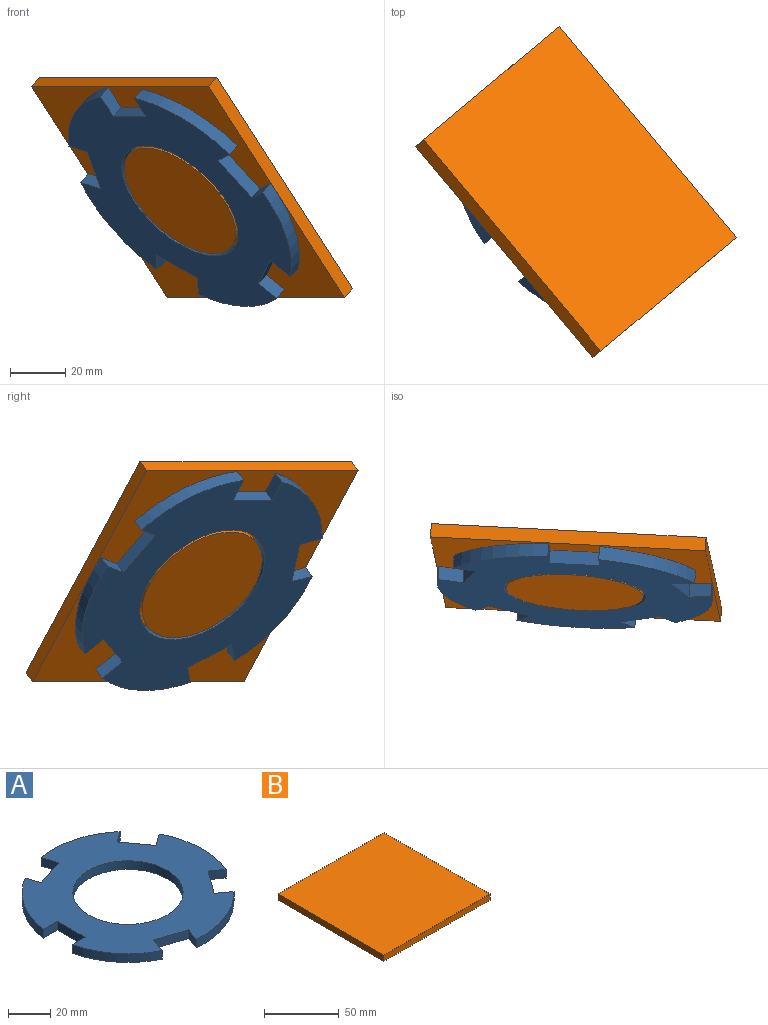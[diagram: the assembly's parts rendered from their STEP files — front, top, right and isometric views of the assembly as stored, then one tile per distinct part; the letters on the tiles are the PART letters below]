
ASSEMBLY  parts=2 mates=1
PART A: 23 faces, bbox 99.5x100x5 mm
  f0: cylinder r=50mm len=41.28mm, axis (0,0,1), area 221.2mm2, adj f2,f5,f16,f18
  f1: plane 8.16x5mm, normal (0.95,0.31,0), area 42.9mm2, adj f3,f16,f17,f18
  f2: plane 8.97x5mm, normal (-0.95,-0.31,0), area 47.1mm2, adj f0,f3,f16,f18
  f3: plane 17.56x5.71mm, normal (-0.31,0.95,0), area 92.3mm2, adj f1,f2,f16,f18
  f4: cylinder r=50mm len=42.77mm, axis (0,0,1), area 221.2mm2, adj f6,f9,f16,f18
  f5: plane 6.94x5.04mm, normal (0.59,-0.81,0), area 42.9mm2, adj f0,f7,f16,f18
  f6: plane 7.63x5.54mm, normal (-0.59,0.81,0), area 47.1mm2, adj f4,f7,f16,f18
  f7: plane 14.94x10.85mm, normal (0.81,0.59,0), area 92.3mm2, adj f5,f6,f16,f18
  f8: cylinder r=50mm len=40.07mm, axis (0,0,1), area 221.2mm2, adj f10,f13,f16,f18
  f9: plane 6.94x5.04mm, normal (-0.59,-0.81,0), area 42.9mm2, adj f4,f11,f16,f18
  f10: plane 7.63x5.54mm, normal (0.59,0.81,0), area 47.1mm2, adj f8,f11,f16,f18
  f11: plane 14.94x10.85mm, normal (0.81,-0.59,0), area 92.3mm2, adj f9,f10,f16,f18
  f12: cylinder r=50mm len=33.44mm, axis (0,0,1), area 221.2mm2, adj f14,f16,f18,f22
  f13: plane 8.16x5mm, normal (-0.95,0.31,0), area 42.9mm2, adj f8,f15,f16,f18
  f14: plane 8.97x5mm, normal (0.95,-0.31,0), area 47.1mm2, adj f12,f15,f16,f18
  f15: plane 17.56x5.71mm, normal (-0.31,-0.95,0), area 92.3mm2, adj f13,f14,f16,f18
  f16: plane 100x99.51mm, normal (0,0,1), area 4846mm2, adj f0,f1,f2,f3,f4,f5,f6,f7
  f17: cylinder r=50mm len=35.76mm, axis (0,0,1), area 221.2mm2, adj f1,f16,f18,f20
  f18: plane 100x99.51mm, normal (0,0,-1), area 4846mm2, adj f0,f1,f2,f3,f4,f5,f6,f7
  f19: cylinder r=26mm len=52mm, axis (0,0,1), area 816.8mm2, adj f16,f18
  f20: plane 9.43x5mm, normal (0,-1,0), area 47.1mm2, adj f16,f17,f18,f21
  f21: plane 18.46x5mm, normal (-1,0,0), area 92.3mm2, adj f16,f18,f20,f22
  f22: plane 8.58x5mm, normal (0,1,0), area 42.9mm2, adj f12,f16,f18,f21
PART B: 8 faces, bbox 100x100x10 mm
  f0: plane 100x5mm, normal (-1,0,0), area 500mm2, adj f1,f3,f4,f5
  f1: plane 100x5mm, normal (0,-1,0), area 500mm2, adj f0,f2,f4,f5
  f2: plane 100x5mm, normal (1,0,0), area 500mm2, adj f1,f3,f4,f5
  f3: plane 100x5mm, normal (0,1,0), area 500mm2, adj f0,f2,f4,f5
  f4: plane 100x100mm, normal (0,0,1), area 10000mm2, adj f0,f1,f2,f3
  f5: plane 100x100mm, normal (0,0,-1), area 8036.5mm2, adj f0,f1,f2,f3,f6
  f6: cylinder r=25mm len=50mm, axis (0,0,1), area 785.4mm2, adj f5,f7
  f7: plane 50x50mm, normal (0,0,-1), area 1963.5mm2, adj f6
PLACE A rot(axis=(-0.28,0.76,0.59),63.2deg) t=(42.8,-127.14,2.48)mm
PLACE B rot(axis=(-0.28,0.76,0.59),63.2deg) t=(42.8,-127.14,2.48)mm
MATE revolute B.f6 <-> A.f0  axis (-0.59,-0.49,-0.64) through (42.8,-127.14,2.48)mm
